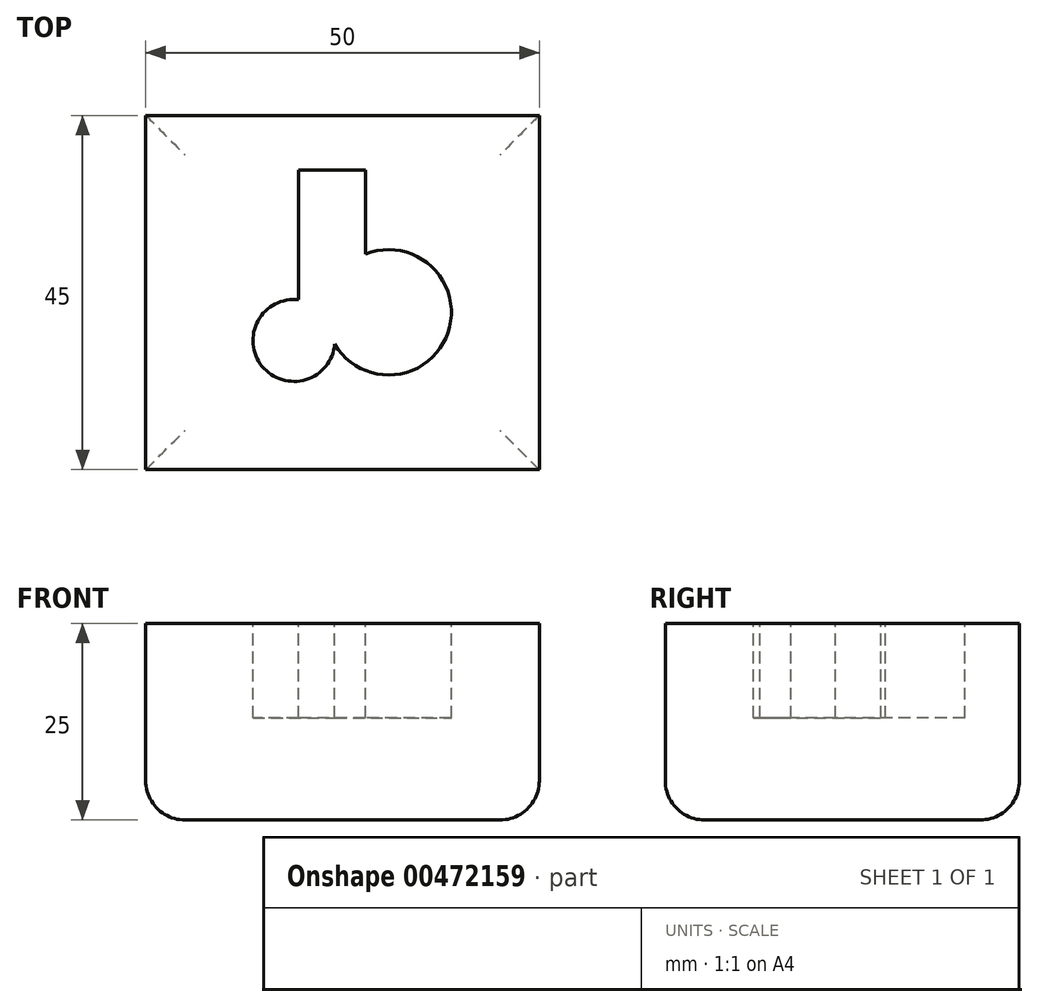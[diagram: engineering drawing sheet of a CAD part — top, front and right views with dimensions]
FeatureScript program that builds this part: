
annotation { "Feature Type Name" : "Feature", "Feature Type Description" : "" }
export const myFeature = defineFeature(function(context is Context, id is Id, definition is map)
    precondition{}
    {
        {
            var Q0;
            Q0=qCreatedBy(makeId("Top.planeOp"),FACE);
            var sketch = newSketch(context, id + "F0", { "sketchPlane" : qUnion([Q0])});
            skLineSegment(sketch, "E0.bottom", {"start": v(-22.5, 25) * mm, "end": v(27.5, 25) * mm});
            skLineSegment(sketch, "E0.top", {"start": v(-22.5, -20) * mm, "end": v(27.5, -20) * mm});
            skLineSegment(sketch, "E0.left", {"start": v(-22.5, 25) * mm, "end": v(-22.5, -20) * mm});
            skLineSegment(sketch, "E0.right", {"start": v(27.5, 25) * mm, "end": v(27.5, -20) * mm});
            skSolve(sketch);
        }
        {
            var Q0;
            Q0 = qSketchRegion(id + "F0", true);
            extrude(context, id + "F1", {"entities" : qUnion([Q0]), "depth" : 25 * mm});
        }
        {
            var Q0;
            Q0=makeQuery(id+"F1.opExtrude","CAP_FACE",FACE,{"disambiguationData":[OSD([sQuery(id+"F0.wireOp",EDGE,"E0.bottom"),sQuery(id+"F0.wireOp",EDGE,"E0.top"),sQuery(id+"F0.wireOp",EDGE,"E0.left"),sQuery(id+"F0.wireOp",EDGE,"E0.right")])],"isStart":false});
            var sketch = newSketch(context, id + "F2", { "sketchPlane" : qUnion([Q0])});
            skCircle(sketch, "E1", {"center": v(-3.66, -3.58) * mm, "radius": 5.2 * mm});
            skCircle(sketch, "E2", {"center": v(8.37, 0) * mm, "radius": 7.96 * mm});
            skLineSegment(sketch, "E3.bottom", {"start": v(5.4, 18.05) * mm, "end": v(-3.08, 18.05) * mm});
            skLineSegment(sketch, "E3.top", {"start": v(5.4, 1.6) * mm, "end": v(-3.08, 1.6) * mm});
            skLineSegment(sketch, "E3.left", {"start": v(5.4, 18.05) * mm, "end": v(5.4, 1.6) * mm});
            skLineSegment(sketch, "E3.right", {"start": v(-3.08, 18.05) * mm, "end": v(-3.08, 1.6) * mm});
            skSolve(sketch);
        }
        {
            var Q0;
            Q0 = qSketchRegion(id + "F2", true);
            extrude(context, id + "F3", {"entities" : qUnion([Q0]), "operationType" : NewBodyOperationType.REMOVE, "oppositeDirection" : true, "depth" : 12 * mm});
        }
        {
            var Q0;
            Q0=makeQuery(id+"F1.opExtrude","CAP_EDGE",EDGE,{"disambiguationData":[OSD([sQuery(id+"F0.wireOp",EDGE,"E0.left")])],"isStart":true});
            var Q1;
            Q1=makeQuery(id+"F1.opExtrude","CAP_FACE",FACE,{"disambiguationData":[OSD([sQuery(id+"F0.wireOp",EDGE,"E0.bottom"),sQuery(id+"F0.wireOp",EDGE,"E0.top"),sQuery(id+"F0.wireOp",EDGE,"E0.left"),sQuery(id+"F0.wireOp",EDGE,"E0.right")])],"isStart":true});
            fillet(context, id + "F4", {"entities" : qUnion([Q0, Q1]), "radius" : 5 * mm, "tangentPropagation" : true, "allowEdgeOverflow" : false});
        }
    });
